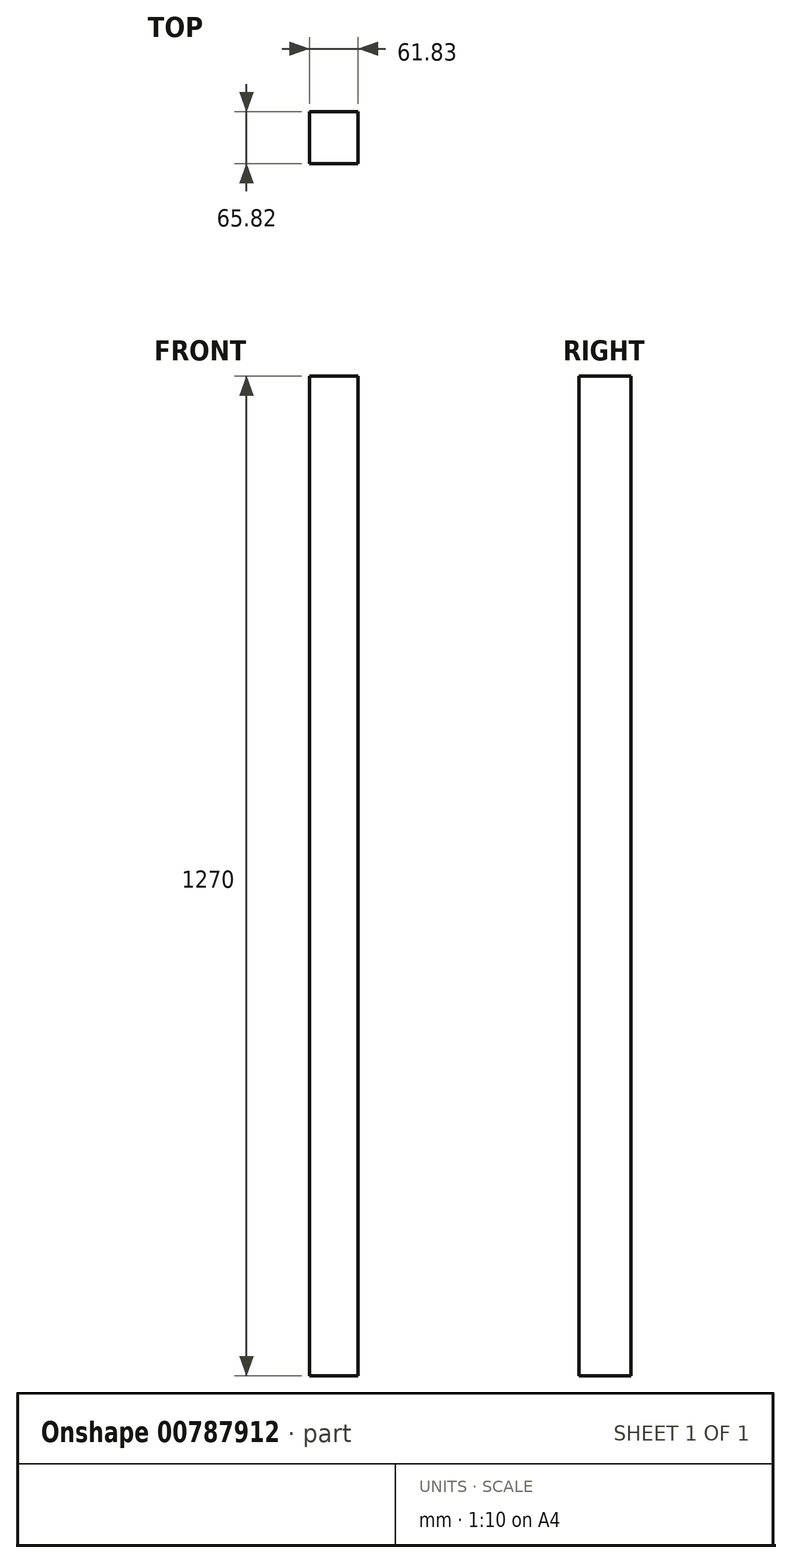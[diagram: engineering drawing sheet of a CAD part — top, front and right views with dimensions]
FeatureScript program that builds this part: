
annotation { "Feature Type Name" : "Feature", "Feature Type Description" : "" }
export const myFeature = defineFeature(function(context is Context, id is Id, definition is map)
    precondition{}
    {
        {
            var Q0;
            Q0=qCreatedBy(makeId("Top.planeOp"),FACE);
            var sketch = newSketch(context, id + "F0", { "sketchPlane" : qUnion([Q0])});
            skLineSegment(sketch, "E0.bottom", {"start": v(0, 0) * mm, "end": v(-61.83, 0) * mm});
            skLineSegment(sketch, "E0.top", {"start": v(0, -65.82) * mm, "end": v(-61.83, -65.82) * mm});
            skLineSegment(sketch, "E0.left", {"start": v(0, 0) * mm, "end": v(0, -65.82) * mm});
            skLineSegment(sketch, "E0.right", {"start": v(-61.83, 0) * mm, "end": v(-61.83, -65.82) * mm});
            skSolve(sketch);
        }
        {
            var Q0;
            Q0 = qSketchRegion(id + "F0", true);
            extrude(context, id + "F1", {"entities" : qUnion([Q0]), "depth" : 1270 * mm, "offsetDistance" : 25.4 * mm});
        }
    });
